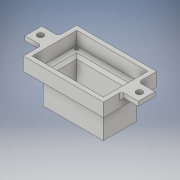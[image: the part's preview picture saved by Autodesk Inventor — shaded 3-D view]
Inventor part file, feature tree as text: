
AUTODESK INVENTOR PART (.ipt)
format: ipt  version: 2019 (Build 230136000, 136)  size: 290,816 bytes
history: native  units: mm
features: extrude x10, sketch x10, projected_geometry x7, chamfer x6, other x1, mirror x1
ambient origin geometry x8: Origin, YZ Plane, XZ Plane, XY Plane, X Axis, Y Axis, Z Axis, Center Point
bodies: Body1 (feature_tree)
feature tree (35):
  other  "Bryła1"
  extrude  "Wyciągnięcie proste1"  Depth=54.0mm
  extrude  "Wyciągnięcie proste2"  Depth=30.0mm
  extrude  "Wyciągnięcie proste3"  Depth=3.0mm TaperAngle=0.0deg
  extrude  "Wyciągnięcie proste4"  Depth=16.1mm
  extrude  "Wyciągnięcie proste5"  Depth=16.1mm
  extrude  "Wyciągnięcie proste6"  Depth=25.5mm
  extrude  "Wyciągnięcie proste7"  Depth=15.0mm
  chamfer  "Faza1"  Distance=15.0mm
  extrude  "Wyciągnięcie proste8"  Depth=14.25mm
  chamfer  "Faza2"  Distance=14.25mm
  extrude  "Wyciągnięcie proste9"  Depth=3.0mm TaperAngle=0.0deg
  extrude  "Wyciągnięcie proste10"  Depth=15.0mm
  mirror  "Odbij1"
  chamfer  "Faza3"  Distance=15.0mm
  chamfer  "Faza4"  Distance=3.0mm
  chamfer  "Faza5"  Distance=3.0mm
  chamfer  "Faza6"  Distance=3.0mm
  sketch  "Szkic3"
  sketch  "Szkic4"
  sketch  "Szkic5"
  projected_geometry  "Pętla rzutowana1"
  sketch  "Szkic6"
  projected_geometry  "Pętla rzutowana2"
  sketch  "Szkic7"
  projected_geometry  "Pętla rzutowana3"
  sketch  "Szkic8"
  sketch  "Szkic9"
  projected_geometry  "Pętla rzutowana4"
  projected_geometry  "Pętla rzutowana5"
  sketch  "Szkic10"
  projected_geometry  "Pętla rzutowana6"
  sketch  "Szkic11"
  projected_geometry  "Pętla rzutowana7"
  sketch  "Szkic12"
